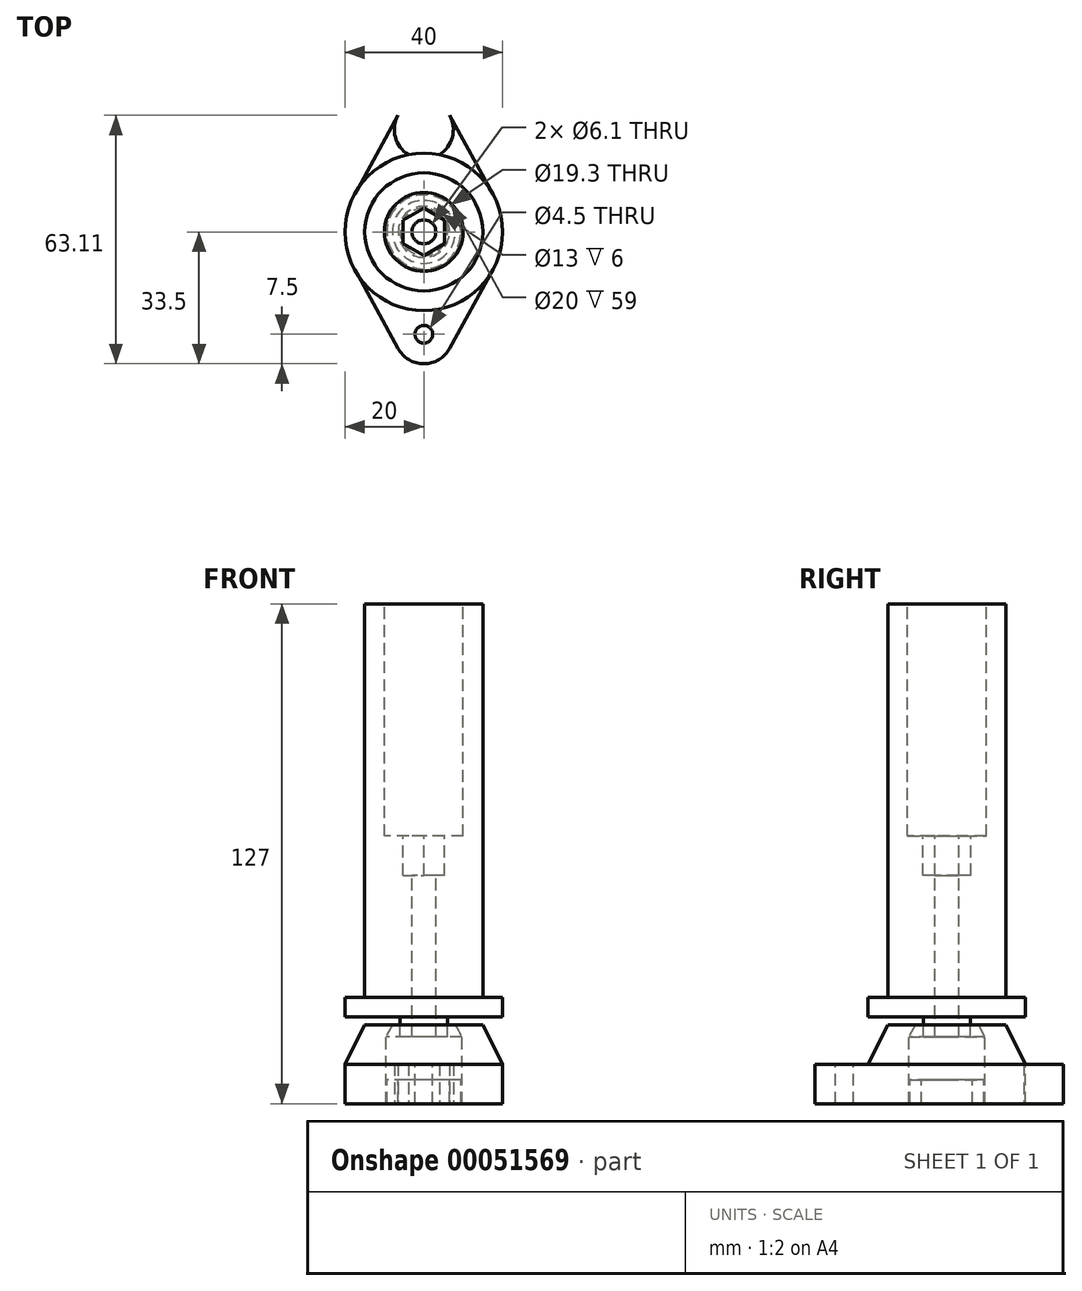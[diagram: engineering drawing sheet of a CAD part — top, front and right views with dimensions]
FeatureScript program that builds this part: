
annotation { "Feature Type Name" : "Feature", "Feature Type Description" : "" }
export const myFeature = defineFeature(function(context is Context, id is Id, definition is map)
    precondition{}
    {
        {
            var Q0;
            Q0=qCreatedBy(makeId("Front.planeOp"),FACE);
            var sketch = newSketch(context, id + "F0", { "sketchPlane" : qUnion([Q0])});
            skLineSegment(sketch, "E0", {"start": v(-20, 0) * mm, "end": v(-20, 5) * mm});
            skLineSegment(sketch, "E1", {"start": v(-20, 5) * mm, "end": v(-15, 5) * mm});
            skLineSegment(sketch, "E2", {"start": v(-15, 5) * mm, "end": v(-15, 105) * mm});
            skLineSegment(sketch, "E3", {"start": v(-15, 105) * mm, "end": v(-10, 105) * mm});
            skLineSegment(sketch, "E4", {"start": v(-10, 105) * mm, "end": v(-10, 46) * mm});
            skLineSegment(sketch, "E5", {"start": v(-10, 46) * mm, "end": v(-3.05, 46) * mm});
            skLineSegment(sketch, "E6", {"start": v(-3.05, 46) * mm, "end": v(-3.05, 0) * mm});
            skLineSegment(sketch, "E7", {"start": v(-3.05, 0) * mm, "end": v(-20, 0) * mm});
            skLineSegment(sketch, "E8", {"start": v(0, 0) * mm, "end": v(0, -22.23) * mm, "construction": true});
            skLineSegment(sketch, "E9", {"start": v(-3.25, 105) * mm, "end": v(-3.25, -19) * mm, "construction": true});
            skLineSegment(sketch, "E10", {"start": v(-3.25, -19) * mm, "end": v(-28.47, -19) * mm, "construction": true});
            skLineSegment(sketch, "E11", {"start": v(-28.47, -19) * mm, "end": v(-28.47, -23.06) * mm, "construction": true});
            skLineSegment(sketch, "E12", {"start": v(-28.47, -23.06) * mm, "end": v(0, -23.06) * mm, "construction": true});
            skLineSegment(sketch, "E13", {"start": v(-6, 0) * mm, "end": v(-6, -5) * mm});
            skLineSegment(sketch, "E14", {"start": v(-6, -5) * mm, "end": v(-3.05, -5) * mm});
            skPoint(sketch, "E15.end.orphan", {"position": v(-3.25, 0) * mm});
            skLineSegment(sketch, "E16", {"start": v(-3.05, 0) * mm, "end": v(-3.05, -5) * mm});
            skLineSegment(sketch, "E17", {"start": v(-9.65, -5) * mm, "end": v(-8, -5) * mm, "construction": true});
            skLineSegment(sketch, "E18", {"start": v(-8, -5) * mm, "end": v(-8, -2) * mm, "construction": true});
            skLineSegment(sketch, "E19", {"start": v(-8, -2) * mm, "end": v(-20, -2) * mm});
            skLineSegment(sketch, "E20", {"start": v(-20, -2) * mm, "end": v(-20, -22) * mm});
            skLineSegment(sketch, "E21", {"start": v(-20, -22) * mm, "end": v(-9.65, -22) * mm});
            skLineSegment(sketch, "E22", {"start": v(-9.65, -22) * mm, "end": v(-9.65, -5) * mm});
            skLineSegment(sketch, "E23.bottom", {"start": v(-9.4, -22) * mm, "end": v(-6.5, -22) * mm});
            skLineSegment(sketch, "E23.top", {"start": v(-9.4, -16) * mm, "end": v(-6.5, -16) * mm});
            skLineSegment(sketch, "E23.left", {"start": v(-9.4, -22) * mm, "end": v(-9.4, -16) * mm});
            skLineSegment(sketch, "E23.right", {"start": v(-6.5, -22) * mm, "end": v(-6.5, -16) * mm});
            skLineSegment(sketch, "E24", {"start": v(-9.65, -5) * mm, "end": v(-8, -2) * mm});
            skSolve(sketch);
        }
        {
            var Q0;
            Q0=makeQuery(id+"F0.imprint","IMPRINT",FACE,{"disambiguationData":[TD([[makeQuery(id+"F0.imprint","IMPRINT",EDGE,{"derivedFrom":sQuery(id+"F0.wireOp",EDGE,"E0")}),-1.0]])]});
            var Q1;
            Q1=sQuery(id+"F0.wireOp",EDGE,"E8");
            revolve(context, id + "F1", {"entities" : qUnion([Q0]), "axis" : qUnion([Q1]), "revolveType" : RevolveType.FULL});
        }
        {
            var Q0;
            Q0=makeQuery(id+"F1.opRevolve","SWEPT_FACE",FACE,{"disambiguationData":[OSD([sQuery(id+"F0.wireOp",EDGE,"E5")])]});
            var sketch = newSketch(context, id + "F2", { "sketchPlane" : qUnion([Q0])});
            skCircle(sketch, "E25.cCircle", {"center": v(0, 0) * mm, "radius": 5.25 * mm, "construction": true});
            skLineSegment(sketch, "E25.0", {"start": v(5.25, -3.03) * mm, "end": v(0, -6.06) * mm});
            skLineSegment(sketch, "E25.1", {"start": v(0, -6.06) * mm, "end": v(-5.25, -3.03) * mm});
            skLineSegment(sketch, "E25.2", {"start": v(-5.25, -3.03) * mm, "end": v(-5.25, 3.03) * mm});
            skLineSegment(sketch, "E25.3", {"start": v(-5.25, 3.03) * mm, "end": v(0, 6.06) * mm});
            skLineSegment(sketch, "E25.4", {"start": v(0, 6.06) * mm, "end": v(5.25, 3.03) * mm});
            skLineSegment(sketch, "E25.5", {"start": v(5.25, 3.03) * mm, "end": v(5.25, -3.03) * mm});
            skSolve(sketch);
        }
        {
            var Q0;
            Q0 = qSketchRegion(id + "F2", true);
            extrude(context, id + "F3", {"entities" : qUnion([Q0]), "operationType" : NewBodyOperationType.REMOVE, "oppositeDirection" : true, "depth" : 10 * mm});
        }
        {
            var Q0;
            {var subQ2=sQuery(id+"F0.wireOp",EDGE,"E13");Q0=makeQuery(id+"F0.imprint","IMPRINT",FACE,{"disambiguationData":[TD([[makeQuery(id+"F0.imprint","IMPRINT",EDGE,{"derivedFrom":subQ2}),1.0]])]});}
            var Q1;
            Q1=sQuery(id+"F0.wireOp",EDGE,"E8");
            revolve(context, id + "F4", {"entities" : qUnion([Q0]), "axis" : qUnion([Q1]), "revolveType" : RevolveType.FULL});
        }
        {
            var Q0;
            Q0=makeQuery(id+"F0.imprint","IMPRINT",FACE,{"disambiguationData":[TD([[makeQuery(id+"F0.imprint","IMPRINT",EDGE,{"derivedFrom":sQuery(id+"F0.wireOp",EDGE,"E17")}),1.0]])]});
            var Q1;
            Q1=makeQuery(id+"F0.imprint","IMPRINT",FACE,{"disambiguationData":[TD([[makeQuery(id+"F0.imprint","IMPRINT",EDGE,{"derivedFrom":sQuery(id+"F0.wireOp",EDGE,"E19")}),1.0]])]});
            var Q2;
            Q2=sQuery(id+"F0.wireOp",EDGE,"E8");
            revolve(context, id + "F5", {"entities" : qUnion([Q0, Q1]), "axis" : qUnion([Q2]), "revolveType" : RevolveType.FULL});
        }
        {
            var Q0;
            Q0=makeQuery(id+"F5.opRevolve","SWEPT_FACE",FACE,{"disambiguationData":[OSD([sQuery(id+"F0.wireOp",EDGE,"E21")])]});
            var sketch = newSketch(context, id + "F6", { "sketchPlane" : qUnion([Q0])});
            skCircle(sketch, "E26", {"center": v(0, 26) * mm, "radius": 7.5 * mm});
            skLineSegment(sketch, "E27", {"start": v(0, 0) * mm, "end": v(42.5, 0) * mm});
            skCircle(sketch, "E28.MirrorC", {"center": v(0, -26) * mm, "radius": 7.5 * mm});
            skLineSegment(sketch, "E29", {"start": v(6.58, 29.6) * mm, "end": v(17.54, 9.62) * mm});
            skLineSegment(sketch, "E30", {"start": v(-6.58, 29.6) * mm, "end": v(-17.54, 9.62) * mm});
            skLineSegment(sketch, "E31.MirrorCS", {"start": v(6.58, -29.6) * mm, "end": v(17.54, -9.62) * mm});
            skLineSegment(sketch, "E32.MirrorCS", {"start": v(-6.58, -29.6) * mm, "end": v(-17.54, -9.62) * mm});
            skSolve(sketch);
        }
        {
            var Q0;
            {var subQ0=sQuery(id+"F6.wireOp",EDGE,"E32.MirrorCS");Q0=makeQuery(id+"F6.imprint","IMPRINT",FACE,{"disambiguationData":[TD([[makeQuery(id+"F6.imprint","IMPRINT",EDGE,{"derivedFrom":subQ0}),-1.0]])]});}
            var Q1;
            {var subQ0=sQuery(id+"F6.wireOp",EDGE,"E28.MirrorC");var subQ1=makeQuery(id+"F6.imprint","INTERSECT",VERTEX,{"derivedFrom":[subQ0,sQuery(id+"F6.wireOp",EDGE,"E31.MirrorCS")]});Q1=makeQuery(id+"F6.imprint","IMPRINT",FACE,{"disambiguationData":[TD([[makeQuery(id+"F6.imprint","IMPRINT",EDGE,{"disambiguationData":[TD([[subQ1,-1.0]])],"derivedFrom":subQ0}),-1.0]])]});}
            var Q2;
            {var subQ0=sQuery(id+"F6.wireOp",EDGE,"E31.MirrorCS");Q2=makeQuery(id+"F6.imprint","IMPRINT",FACE,{"disambiguationData":[TD([[makeQuery(id+"F6.imprint","IMPRINT",EDGE,{"derivedFrom":subQ0}),1.0]])]});}
            var Q3;
            {var subQ0=sQuery(id+"F6.wireOp",EDGE,"E26");var subQ1=makeQuery(id+"F6.imprint","INTERSECT",VERTEX,{"derivedFrom":[subQ0,sQuery(id+"F6.wireOp",EDGE,"E29")]});Q3=makeQuery(id+"F6.imprint","IMPRINT",FACE,{"disambiguationData":[TD([[makeQuery(id+"F6.imprint","IMPRINT",EDGE,{"disambiguationData":[TD([[subQ1,-1.0]])],"derivedFrom":subQ0}),1.0]])]});}
            var Q4;
            {var subQ0=sQuery(id+"F6.wireOp",EDGE,"E29");Q4=makeQuery(id+"F6.imprint","IMPRINT",FACE,{"disambiguationData":[TD([[makeQuery(id+"F6.imprint","IMPRINT",EDGE,{"derivedFrom":subQ0}),-1.0]])]});}
            var Q5;
            {var subQ0=sQuery(id+"F6.wireOp",EDGE,"E30");Q5=makeQuery(id+"F6.imprint","IMPRINT",FACE,{"disambiguationData":[TD([[makeQuery(id+"F6.imprint","IMPRINT",EDGE,{"derivedFrom":subQ0}),1.0]])]});}
            var Q6;
            Q6=makeQuery(id+"F5.opRevolve","SWEPT_FACE",FACE,{"disambiguationData":[OSD([sQuery(id+"F0.wireOp",EDGE,"E19")])]});
            extrude(context, id + "F7", {"entities" : qUnion([Q0, Q1, Q2, Q3, Q4, Q5]), "operationType" : NewBodyOperationType.ADD, "oppositeDirection" : true, "endBoundEntityFace" : qUnion([Q6]), "depth" : 10 * mm});
        }
        {
            var Q0;
            Q0=makeQuery(id+"F0.imprint","IMPRINT",FACE,{"disambiguationData":[TD([[makeQuery(id+"F0.imprint","IMPRINT",EDGE,{"derivedFrom":sQuery(id+"F0.wireOp",EDGE,"E23.bottom")}),1.0]])]});
            var Q1;
            Q1=sQuery(id+"F0.wireOp",EDGE,"E8");
            revolve(context, id + "F11", {"entities" : qUnion([Q0]), "axis" : qUnion([Q1]), "revolveType" : RevolveType.FULL});
        }
        {
            var Q0;
            Q0=makeQuery(id+"F7.opExtrude","CAP_FACE",FACE,{"disambiguationData":[OSD([sQuery(id+"F0.wireOp",EDGE,"E20"),sQuery(id+"F0.wireOp",EDGE,"E21"),sQuery(id+"F6.wireOp",EDGE,"E26"),sQuery(id+"F6.wireOp",EDGE,"E29"),sQuery(id+"F6.wireOp",EDGE,"E30")])],"isStart":false});
            var sketch = newSketch(context, id + "F8", { "sketchPlane" : qUnion([Q0])});
            skPoint(sketch, "E33", {"position": v(0, -26) * mm});
            skPoint(sketch, "E34", {"position": v(0, 25) * mm});
            skSolve(sketch);
        }
        {
            var Q0;
            Q0=sQuery(id+"F8.wireOp",VERTEX,"E33");
            var Q1;
            Q1=sQuery(id+"F8.wireOp",VERTEX,"E34");
            var Q2;
            Q2=makeQuery(id+"F5.opRevolve","SWEPT_BODY",BODY,{"disambiguationData":[OSD([sQuery(id+"F0.wireOp",EDGE,"E17"),sQuery(id+"F0.wireOp",EDGE,"E18"),sQuery(id+"F0.wireOp",EDGE,"E19"),sQuery(id+"F0.wireOp",EDGE,"E20"),sQuery(id+"F0.wireOp",EDGE,"E21"),sQuery(id+"F0.wireOp",EDGE,"E22")])]});
            hole(context, id + "F9", {"style" : HoleStyle.SIMPLE, "holeDiameter" : 4.5 * mm, "endStyle" : HoleEndStyle.THROUGH, "locations" : qUnion([Q0, Q1]), "scope" : qUnion([Q2])});
        }
        {
            var Q0;
            Q0=makeQuery(id+"F5.opRevolve","SWEPT_EDGE",EDGE,{"disambiguationData":[OSD([sQuery(id+"F0.wireOp",EDGE,"E19"),sQuery(id+"F0.wireOp",EDGE,"E20")])]});
            chamfer(context, id + "F10", {"entities" : qUnion([Q0]), "chamferType" : ChamferType.TWO_OFFSETS, "width1" : 5 * mm, "oppositeDirection" : false, "width2" : 10 * mm, "tangentPropagation" : true});
        }
    });
